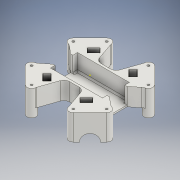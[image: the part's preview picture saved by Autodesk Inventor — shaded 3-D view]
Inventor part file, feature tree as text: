
AUTODESK INVENTOR PART (.ipt)
format: ipt  version: 2020 (Build 240168000, 168)  size: 553,984 bytes
history: native  units: mm
features: sketch x10, extrude x9, projected_geometry x6, fillet x3, other x1, mirror x1
ambient origin geometry x8: Origin, YZ Plane, XZ Plane, XY Plane, X Axis, Y Axis, Z Axis, Center Point
bodies: Body1 (feature_tree)
feature tree (30):
  other  "floor_v2.ipt"
  extrude  "Выдавливание2"  Depth=10.0mm
  extrude  "Выдавливание3"  Depth=12.0mm
  mirror  "Зеркальное отражение1"
  sketch  "Эскиз8"
  sketch  "Эскиз9"
  extrude  "Выдавливание4"  Depth=34.65mm TaperAngle=0.0deg
  extrude  "Выдавливание5"  Depth=20.3mm
  sketch  "Эскиз10"
  extrude  "Выдавливание6"  Depth=10.15mm TaperAngle=0.0deg
  sketch  "Эскиз11"
  extrude  "Выдавливание7"  Depth=9.0mm TaperAngle=0.0deg
  extrude  "Выдавливание10"  Depth=7.0mm TaperAngle=0.0deg
  fillet  "Сопряжение1"  Radius=70.45mm
  fillet  "Сопряжение2"  Radius=36.65mm
  extrude  "Выдавливание11"  Depth=76.45mm
  extrude  "Выдавливание12"  Depth=42.65mm
  fillet  "Сопряжение3"  Radius=3.225mm
  sketch  "Эскиз3"
  sketch  "Эскиз6"
  sketch  "Эскиз7"
  sketch  "Эскиз12"
  projected_geometry  "Спроецированная петля2"
  projected_geometry  "Спроецированная петля3"
  projected_geometry  "Спроецированная петля4"
  projected_geometry  "Спроецированная петля5"
  sketch  "Эскиз13"
  projected_geometry  "Спроецированная петля6"
  sketch  "Эскиз14"
  projected_geometry  "Спроецированная петля7"
